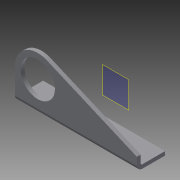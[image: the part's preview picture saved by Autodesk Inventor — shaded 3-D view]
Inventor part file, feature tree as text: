
AUTODESK INVENTOR PART (.ipt)
format: ipt  version: 2013 (Build 170138000, 138)  size: 167,424 bytes
history: native  units: in
note: dims shown in document units (in); Inventor stores cm internally (conversion verified against a paired STEP export)
features: other x7, sheet_metal_op x6, sketch x6, reference x2, plane x1
ambient origin geometry x8: Origin, YZ Plane, XZ Plane, XY Plane, X Axis, Y Axis, Z Axis, Center Point
bodies: Solid1 (feature_tree)
feature tree (22):
  sheet_metal_op  "Face1"
  plane  "Work Plane1"
  sheet_metal_op  "Flange2"
  sheet_metal_op  "Face2"
  sketch  "Sketch1"  dims[d2=0.266in d3=0.266in]
  other  "Plate1"
  sketch  "Sketch4"  dims[d9=0.125in]
  other  "Plate3"
  sheet_metal_op  "Bend2"
  sheet_metal_op  "Corner2"
  sketch  "Sketch5"  dims[d26=0.75in]
  sketch  "Sketch6"  dims[d27=4.0in]
  other  "Plate4"
  sheet_metal_op  "Bend3"
  sketch  "Sketch7"  dims[d28=0.125in]
  reference  "Reference1"
  reference  "Reference2"
  sketch  "Sketch8"  dims[d29=0.0625in d30=0.25in d31=0.125in d32=1.75in d33=90.0deg d34=0.05in d35=0.5in d36=0.125in d37=0.125in d42=0.25in d43=0.125in d44=0.0in d45=0.125in d46=0.125in d47=0.0625in d48=0.25in d49=0.125in d50=0.125in d51=0.0in d52=1.125in d53=0.125in d54=0.0in]
  other  "Cut3"
  other  "Cut4"
  other  "Cut5"
  other  "Definition1"
